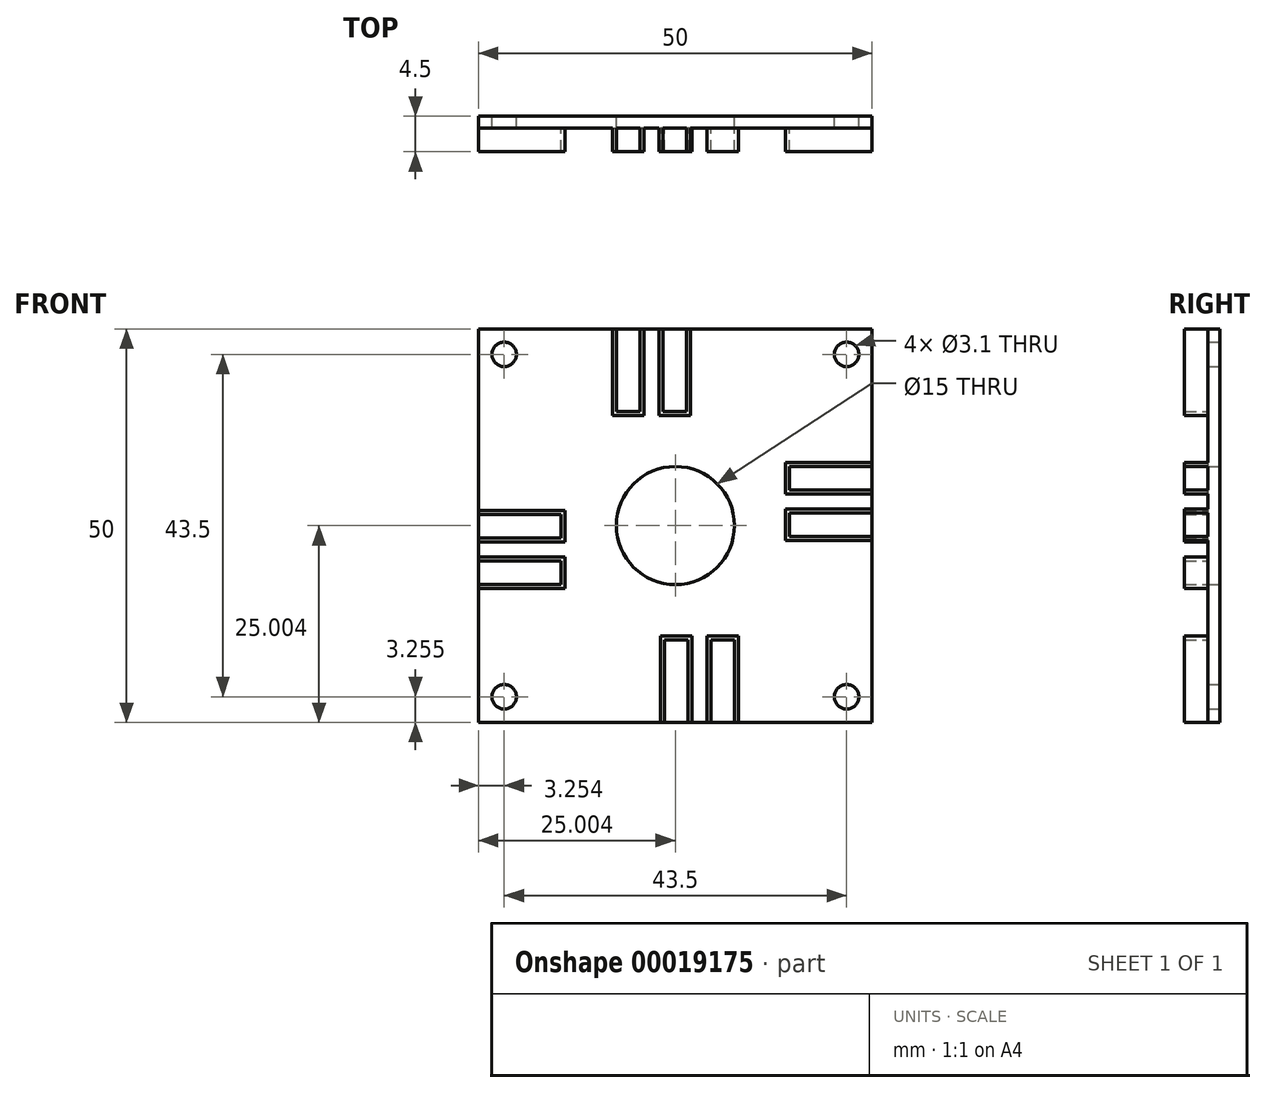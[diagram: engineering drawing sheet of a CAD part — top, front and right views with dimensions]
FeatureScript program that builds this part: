
annotation { "Feature Type Name" : "Feature", "Feature Type Description" : "" }
export const myFeature = defineFeature(function(context is Context, id is Id, definition is map)
    precondition{}
    {
        {
            var Q0;
            Q0=qCreatedBy(makeId("Front.planeOp"),FACE);
            var sketch = newSketch(context, id + "F0", { "sketchPlane" : qUnion([Q0])});
            skLineSegment(sketch, "E0.bottom", {"start": v(-18.96, 21.51) * mm, "end": v(31.04, 21.51) * mm});
            skLineSegment(sketch, "E0.top", {"start": v(-18.96, -28.49) * mm, "end": v(31.04, -28.49) * mm});
            skLineSegment(sketch, "E0.left", {"start": v(-18.96, 21.51) * mm, "end": v(-18.96, -28.49) * mm});
            skLineSegment(sketch, "E0.right", {"start": v(31.04, 21.51) * mm, "end": v(31.04, -28.49) * mm});
            skLineSegment(sketch, "E1", {"start": v(-18.96, -28.49) * mm, "end": v(31.04, 21.51) * mm, "construction": true});
            skLineSegment(sketch, "E2", {"start": v(-18.96, 21.51) * mm, "end": v(31.04, -28.49) * mm, "construction": true});
            skLineSegment(sketch, "E3", {"start": v(-18.96, -3.49) * mm, "end": v(31.04, -3.49) * mm, "construction": true});
            skLineSegment(sketch, "E4", {"start": v(6.04, 21.51) * mm, "end": v(6.04, -28.49) * mm, "construction": true});
            skCircle(sketch, "E5", {"center": v(6.04, -3.49) * mm, "radius": 7.5 * mm});
            skCircle(sketch, "E6", {"center": v(27.8, 18.26) * mm, "radius": 1.55 * mm});
            skCircle(sketch, "E7", {"center": v(-15.7, 18.26) * mm, "radius": 1.55 * mm});
            skCircle(sketch, "E8", {"center": v(-15.7, -25.24) * mm, "radius": 1.55 * mm});
            skCircle(sketch, "E9", {"center": v(27.8, -25.24) * mm, "radius": 1.55 * mm});
            skSolve(sketch);
        }
        {
            var Q0;
            Q0=makeQuery(id+"F0.imprint","IMPRINT",FACE,{"disambiguationData":[TD([[makeQuery(id+"F0.imprint","IMPRINT",EDGE,{"derivedFrom":sQuery(id+"F0.wireOp",EDGE,"E0.bottom")}),-1.0]])]});
            extrude(context, id + "F1", {"entities" : qUnion([Q0]), "depth" : 1.5 * mm});
        }
        {
            var Q0;
            Q0=makeQuery(id+"F1.opExtrude","CAP_FACE",FACE,{"disambiguationData":[OSD([sQuery(id+"F0.wireOp",EDGE,"E0.bottom"),sQuery(id+"F0.wireOp",EDGE,"E0.top"),sQuery(id+"F0.wireOp",EDGE,"E0.left"),sQuery(id+"F0.wireOp",EDGE,"E0.right"),sQuery(id+"F0.wireOp",EDGE,"E5"),sQuery(id+"F0.wireOp",EDGE,"E6"),sQuery(id+"F0.wireOp",EDGE,"E7"),sQuery(id+"F0.wireOp",EDGE,"E8"),sQuery(id+"F0.wireOp",EDGE,"E9")])],"isStart":false});
            var sketch = newSketch(context, id + "F2", { "sketchPlane" : qUnion([Q0])});
            skLineSegment(sketch, "E10.bottom", {"start": v(4.64, -28.49) * mm, "end": v(7.64, -28.49) * mm});
            skLineSegment(sketch, "E10.top", {"start": v(4.64, -17.99) * mm, "end": v(7.64, -17.99) * mm});
            skLineSegment(sketch, "E10.left", {"start": v(4.64, -28.49) * mm, "end": v(4.64, -17.99) * mm});
            skLineSegment(sketch, "E10.right", {"start": v(7.64, -28.49) * mm, "end": v(7.64, -17.99) * mm});
            skLineSegment(sketch, "E11.bottom", {"start": v(10.54, -17.99) * mm, "end": v(13.54, -17.99) * mm});
            skLineSegment(sketch, "E11.top", {"start": v(10.54, -28.49) * mm, "end": v(13.54, -28.49) * mm});
            skLineSegment(sketch, "E11.left", {"start": v(10.54, -17.99) * mm, "end": v(10.54, -28.49) * mm});
            skLineSegment(sketch, "E11.right", {"start": v(13.54, -17.99) * mm, "end": v(13.54, -28.49) * mm});
            skLineSegment(sketch, "E12.bottom", {"start": v(4.14, -17.49) * mm, "end": v(8.14, -17.49) * mm});
            skLineSegment(sketch, "E12.top", {"start": v(4.14, -28.49) * mm, "end": v(8.14, -28.49) * mm});
            skLineSegment(sketch, "E12.left", {"start": v(4.14, -17.49) * mm, "end": v(4.14, -28.49) * mm});
            skLineSegment(sketch, "E12.right", {"start": v(8.14, -17.49) * mm, "end": v(8.14, -28.49) * mm});
            skLineSegment(sketch, "E13.bottom", {"start": v(10.04, -17.49) * mm, "end": v(14.04, -17.49) * mm});
            skLineSegment(sketch, "E13.top", {"start": v(10.04, -28.49) * mm, "end": v(14.04, -28.49) * mm});
            skLineSegment(sketch, "E13.left", {"start": v(10.04, -17.49) * mm, "end": v(10.04, -28.49) * mm});
            skLineSegment(sketch, "E13.right", {"start": v(14.04, -17.49) * mm, "end": v(14.04, -28.49) * mm});
            skSolve(sketch);
        }
        {
            var Q0;
            Q0=makeQuery(id+"F2.imprint","IMPRINT",FACE,{"disambiguationData":[TD([[makeQuery(id+"F2.imprint","IMPRINT",EDGE,{"derivedFrom":sQuery(id+"F2.wireOp",EDGE,"E10.top")}),1.0]])]});
            var Q1;
            Q1=makeQuery(id+"F2.imprint","IMPRINT",FACE,{"disambiguationData":[TD([[makeQuery(id+"F2.imprint","IMPRINT",EDGE,{"derivedFrom":sQuery(id+"F2.wireOp",EDGE,"E11.bottom")}),1.0]])]});
            extrude(context, id + "F3", {"entities" : qUnion([Q0, Q1]), "operationType" : NewBodyOperationType.ADD, "depth" : 3 * mm});
        }
        {
            var Q0;
            Q0=qCreatedBy(makeId("Front.planeOp"),FACE);
            var sketch = newSketch(context, id + "F4", { "sketchPlane" : qUnion([Q0])});
            skLineSegment(sketch, "E14.bottom", {"start": v(-18.96, -2.09) * mm, "end": v(-8.46, -2.09) * mm});
            skLineSegment(sketch, "E14.top", {"start": v(-18.96, -5.09) * mm, "end": v(-8.46, -5.09) * mm});
            skLineSegment(sketch, "E14.left", {"start": v(-18.96, -2.09) * mm, "end": v(-18.96, -5.09) * mm});
            skLineSegment(sketch, "E14.right", {"start": v(-8.46, -2.09) * mm, "end": v(-8.46, -5.09) * mm});
            skLineSegment(sketch, "E15.bottom", {"start": v(-18.96, -7.99) * mm, "end": v(-8.46, -7.99) * mm});
            skLineSegment(sketch, "E15.top", {"start": v(-18.96, -10.99) * mm, "end": v(-8.46, -10.99) * mm});
            skLineSegment(sketch, "E15.left", {"start": v(-18.96, -7.99) * mm, "end": v(-18.96, -10.99) * mm});
            skLineSegment(sketch, "E15.right", {"start": v(-8.46, -7.99) * mm, "end": v(-8.46, -10.99) * mm});
            skLineSegment(sketch, "E16.bottom", {"start": v(-18.96, -7.49) * mm, "end": v(-7.96, -7.49) * mm});
            skLineSegment(sketch, "E16.top", {"start": v(-18.96, -11.49) * mm, "end": v(-7.96, -11.49) * mm});
            skLineSegment(sketch, "E16.left", {"start": v(-18.96, -7.49) * mm, "end": v(-18.96, -11.49) * mm});
            skLineSegment(sketch, "E16.right", {"start": v(-7.96, -7.49) * mm, "end": v(-7.96, -11.49) * mm});
            skLineSegment(sketch, "E17.bottom", {"start": v(-18.96, -1.59) * mm, "end": v(-7.96, -1.59) * mm});
            skLineSegment(sketch, "E17.top", {"start": v(-18.96, -5.59) * mm, "end": v(-7.96, -5.59) * mm});
            skLineSegment(sketch, "E17.left", {"start": v(-18.96, -1.59) * mm, "end": v(-18.96, -5.59) * mm});
            skLineSegment(sketch, "E17.right", {"start": v(-7.96, -1.59) * mm, "end": v(-7.96, -5.59) * mm});
            skLineSegment(sketch, "E18.bottom", {"start": v(-1.46, 21.51) * mm, "end": v(1.54, 21.51) * mm});
            skLineSegment(sketch, "E18.top", {"start": v(-1.46, 11.01) * mm, "end": v(1.54, 11.01) * mm});
            skLineSegment(sketch, "E18.left", {"start": v(-1.46, 21.51) * mm, "end": v(-1.46, 11.01) * mm});
            skLineSegment(sketch, "E18.right", {"start": v(1.54, 21.51) * mm, "end": v(1.54, 11.01) * mm});
            skLineSegment(sketch, "E19.bottom", {"start": v(4.44, 21.51) * mm, "end": v(7.44, 21.51) * mm});
            skLineSegment(sketch, "E19.top", {"start": v(4.44, 11.01) * mm, "end": v(7.44, 11.01) * mm});
            skLineSegment(sketch, "E19.left", {"start": v(4.44, 21.51) * mm, "end": v(4.44, 11.01) * mm});
            skLineSegment(sketch, "E19.right", {"start": v(7.44, 21.51) * mm, "end": v(7.44, 11.01) * mm});
            skLineSegment(sketch, "E20.bottom", {"start": v(-1.96, 21.51) * mm, "end": v(2.04, 21.51) * mm});
            skLineSegment(sketch, "E20.top", {"start": v(-1.96, 10.51) * mm, "end": v(2.04, 10.51) * mm});
            skLineSegment(sketch, "E20.left", {"start": v(-1.96, 21.51) * mm, "end": v(-1.96, 10.51) * mm});
            skLineSegment(sketch, "E20.right", {"start": v(2.04, 21.51) * mm, "end": v(2.04, 10.51) * mm});
            skLineSegment(sketch, "E21.bottom", {"start": v(3.94, 21.51) * mm, "end": v(7.94, 21.51) * mm});
            skLineSegment(sketch, "E21.top", {"start": v(3.94, 10.51) * mm, "end": v(7.94, 10.51) * mm});
            skLineSegment(sketch, "E21.left", {"start": v(3.94, 21.51) * mm, "end": v(3.94, 10.51) * mm});
            skLineSegment(sketch, "E21.right", {"start": v(7.94, 21.51) * mm, "end": v(7.94, 10.51) * mm});
            skLineSegment(sketch, "E22.bottom", {"start": v(31.04, 4.01) * mm, "end": v(20.54, 4.01) * mm});
            skLineSegment(sketch, "E22.top", {"start": v(31.04, 1.01) * mm, "end": v(20.54, 1.01) * mm});
            skLineSegment(sketch, "E22.left", {"start": v(31.04, 4.01) * mm, "end": v(31.04, 1.01) * mm});
            skLineSegment(sketch, "E22.right", {"start": v(20.54, 4.01) * mm, "end": v(20.54, 1.01) * mm});
            skLineSegment(sketch, "E23.bottom", {"start": v(31.04, -1.89) * mm, "end": v(20.54, -1.89) * mm});
            skLineSegment(sketch, "E23.top", {"start": v(31.04, -4.89) * mm, "end": v(20.54, -4.89) * mm});
            skLineSegment(sketch, "E23.left", {"start": v(31.04, -1.89) * mm, "end": v(31.04, -4.89) * mm});
            skLineSegment(sketch, "E23.right", {"start": v(20.54, -1.89) * mm, "end": v(20.54, -4.89) * mm});
            skLineSegment(sketch, "E24.bottom", {"start": v(31.04, -1.39) * mm, "end": v(20.04, -1.39) * mm});
            skLineSegment(sketch, "E24.top", {"start": v(31.04, -5.39) * mm, "end": v(20.04, -5.39) * mm});
            skLineSegment(sketch, "E24.left", {"start": v(31.04, -1.39) * mm, "end": v(31.04, -5.39) * mm});
            skLineSegment(sketch, "E24.right", {"start": v(20.04, -1.39) * mm, "end": v(20.04, -5.39) * mm});
            skLineSegment(sketch, "E25.bottom", {"start": v(31.04, 0.51) * mm, "end": v(20.04, 0.51) * mm});
            skLineSegment(sketch, "E25.top", {"start": v(31.04, 4.51) * mm, "end": v(20.04, 4.51) * mm});
            skLineSegment(sketch, "E25.left", {"start": v(31.04, 0.51) * mm, "end": v(31.04, 4.51) * mm});
            skLineSegment(sketch, "E25.right", {"start": v(20.04, 0.51) * mm, "end": v(20.04, 4.51) * mm});
            skSolve(sketch);
        }
        {
            var Q0;
            Q0=makeQuery(id+"F4.imprint","IMPRINT",FACE,{"disambiguationData":[TD([[makeQuery(id+"F4.imprint","IMPRINT",EDGE,{"derivedFrom":sQuery(id+"F4.wireOp",EDGE,"E18.top")}),-1.0]])]});
            extrude(context, id + "F5", {"entities" : qUnion([Q0]), "operationType" : NewBodyOperationType.ADD, "depth" : 4.5 * mm});
        }
        {
            var Q0;
            {var subQ2=sQuery(id+"F4.wireOp",EDGE,"E22.bottom");Q0=makeQuery(id+"F4.imprint","IMPRINT",FACE,{"disambiguationData":[TD([[makeQuery(id+"F4.imprint","IMPRINT",EDGE,{"derivedFrom":subQ2}),-1.0]])]});}
            var Q1;
            Q1=makeQuery(id+"F4.imprint","IMPRINT",FACE,{"disambiguationData":[TD([[makeQuery(id+"F4.imprint","IMPRINT",EDGE,{"derivedFrom":sQuery(id+"F4.wireOp",EDGE,"E19.top")}),-1.0]])]});
            extrude(context, id + "F6", {"entities" : qUnion([Q0, Q1]), "operationType" : NewBodyOperationType.ADD, "depth" : 4.5 * mm});
        }
        {
            var Q0;
            {var subQ4=sQuery(id+"F4.wireOp",EDGE,"E23.bottom");Q0=makeQuery(id+"F4.imprint","IMPRINT",FACE,{"disambiguationData":[TD([[makeQuery(id+"F4.imprint","IMPRINT",EDGE,{"derivedFrom":subQ4}),-1.0]])]});}
            var Q1;
            {var subQ4=sQuery(id+"F4.wireOp",EDGE,"E14.bottom");Q1=makeQuery(id+"F4.imprint","IMPRINT",FACE,{"disambiguationData":[TD([[makeQuery(id+"F4.imprint","IMPRINT",EDGE,{"derivedFrom":subQ4}),1.0]])]});}
            var Q2;
            {var subQ4=sQuery(id+"F4.wireOp",EDGE,"E15.bottom");Q2=makeQuery(id+"F4.imprint","IMPRINT",FACE,{"disambiguationData":[TD([[makeQuery(id+"F4.imprint","IMPRINT",EDGE,{"derivedFrom":subQ4}),1.0]])]});}
            extrude(context, id + "F7", {"entities" : qUnion([Q0, Q1, Q2]), "operationType" : NewBodyOperationType.ADD, "depth" : 4.5 * mm});
        }
    });
